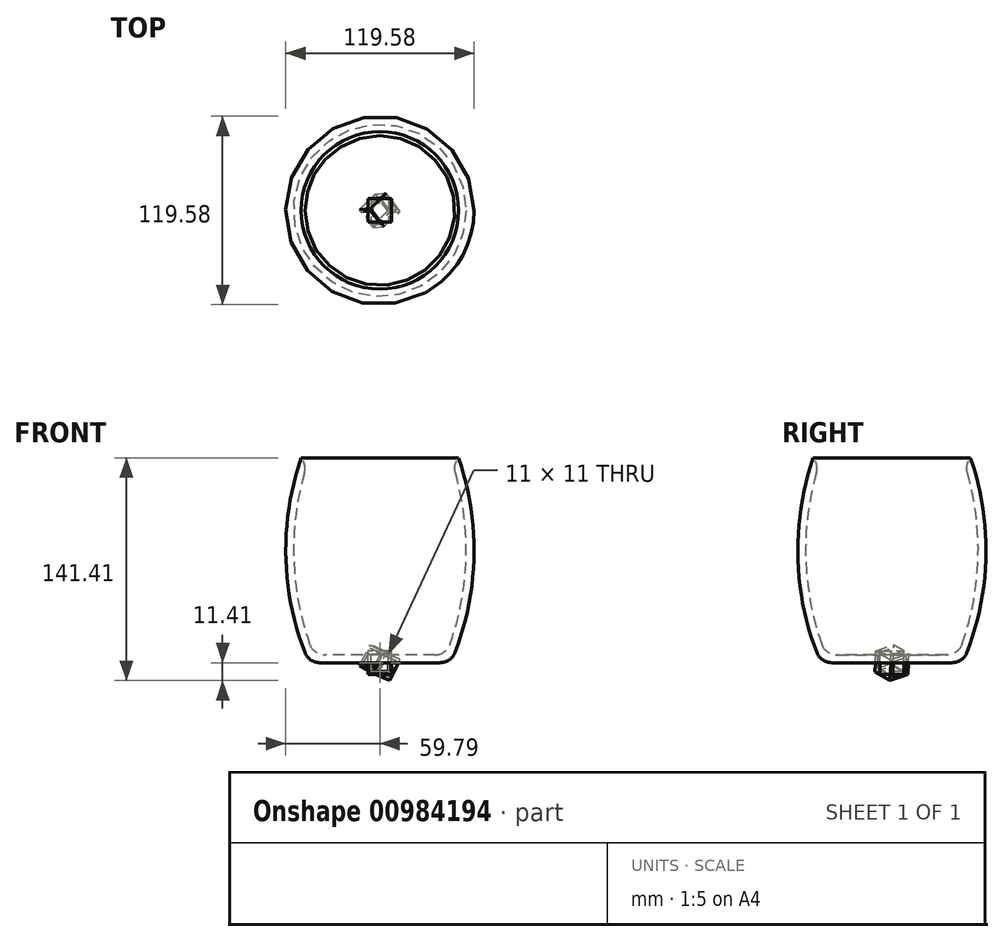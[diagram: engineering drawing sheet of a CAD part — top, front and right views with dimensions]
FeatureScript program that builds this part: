
annotation { "Feature Type Name" : "Feature", "Feature Type Description" : "" }
export const myFeature = defineFeature(function(context is Context, id is Id, definition is map)
    precondition{}
    {
        {
            var Q0;
            Q0=qCreatedBy(makeId("Front.planeOp"),FACE);
            var sketch = newSketch(context, id + "F0", { "sketchPlane" : qUnion([Q0])});
            skLineSegment(sketch, "E0.bottom", {"start": v(7.5, -7.5) * mm, "end": v(-7.5, -7.5) * mm});
            skLineSegment(sketch, "E0.top", {"start": v(7.5, 7.5) * mm, "end": v(-7.5, 7.5) * mm});
            skLineSegment(sketch, "E0.left", {"start": v(7.5, -7.5) * mm, "end": v(7.5, 7.5) * mm});
            skLineSegment(sketch, "E0.right", {"start": v(-7.5, -7.5) * mm, "end": v(-7.5, 7.5) * mm});
            skPoint(sketch, "E0.middle", {"position": v(0, 0) * mm});
            skLineSegment(sketch, "E1.bottom", {"start": v(5.5, -5.5) * mm, "end": v(-5.5, -5.5) * mm});
            skLineSegment(sketch, "E1.top", {"start": v(5.5, 5.5) * mm, "end": v(-5.5, 5.5) * mm});
            skLineSegment(sketch, "E1.left", {"start": v(5.5, -5.5) * mm, "end": v(5.5, 5.5) * mm});
            skLineSegment(sketch, "E1.right", {"start": v(-5.5, -5.5) * mm, "end": v(-5.5, 5.5) * mm});
            skLineSegment(sketch, "E2", {"start": v(0, 0) * mm, "end": v(0, -3) * mm, "construction": true});
            skSolve(sketch);
        }
        {
            var Q0;
            Q0=makeQuery(id+"F0.imprint","IMPRINT",FACE,{"disambiguationData":[TD([[makeQuery(id+"F0.imprint","IMPRINT",EDGE,{"derivedFrom":sQuery(id+"F0.wireOp",EDGE,"E0.bottom")}),-1.0]])]});
            var Q1;
            Q1=makeQuery(id+"F0.imprint","IMPRINT",FACE,{"disambiguationData":[TD([[makeQuery(id+"F0.imprint","IMPRINT",EDGE,{"derivedFrom":sQuery(id+"F0.wireOp",EDGE,"E1.bottom")}),-1.0]])]});
            extrude(context, id + "F1", {"entities" : qUnion([Q0, Q1]), "endBound" : BoundingType.SYMMETRIC, "depth" : 15 * mm, "offsetDistance" : 25 * mm});
        }
        {
            var Q0;
            Q0=makeQuery(id+"F1.opExtrude","CAP_VERTEX",VERTEX,{"disambiguationData":[OSD([sQuery(id+"F0.wireOp",EDGE,"E0.top"),sQuery(id+"F0.wireOp",EDGE,"E0.left")])],"isStart":false});
            var Q1;
            Q1=makeQuery(id+"F1.opExtrude","CAP_VERTEX",VERTEX,{"disambiguationData":[OSD([sQuery(id+"F0.wireOp",EDGE,"E0.bottom"),sQuery(id+"F0.wireOp",EDGE,"E0.right")])],"isStart":true});
            var Q2;
            Q2=makeQuery(id+"F1.opExtrude","CAP_VERTEX",VERTEX,{"disambiguationData":[OSD([sQuery(id+"F0.wireOp",EDGE,"E0.top"),sQuery(id+"F0.wireOp",EDGE,"E0.right")])],"isStart":true});
            cPlane(context, id + "F2", {"entities" : qUnion([Q0, Q1, Q2]), "cplaneType" : CPlaneType.THREE_POINT, "offset" : 25 * mm, "width" : 150 * mm, "height" : 150 * mm});
        }
        {
            var Q0;
            Q0=qCreatedBy(id+"F2.planeOp",FACE);
            var sketch = newSketch(context, id + "F3", { "sketchPlane" : qUnion([Q0])});
            skPoint(sketch, "E3.0", {"position": v(10.6, 7.5) * mm});
            skPoint(sketch, "E4.0", {"position": v(-10.6, -7.5) * mm});
            skLineSegment(sketch, "E5", {"start": v(10.6, 7.5) * mm, "end": v(-10.6, -7.5) * mm, "construction": true});
            skSolve(sketch);
        }
        {
            var Q0;
            Q0=makeQuery(id+"F0.imprint","IMPRINT",FACE,{"disambiguationData":[TD([[makeQuery(id+"F0.imprint","IMPRINT",EDGE,{"derivedFrom":sQuery(id+"F0.wireOp",EDGE,"E1.bottom")}),-1.0]])]});
            extrude(context, id + "F4", {"entities" : qUnion([Q0]), "operationType" : NewBodyOperationType.REMOVE, "endBound" : BoundingType.SYMMETRIC, "oppositeDirection" : true, "depth" : 15 * mm, "offsetDistance" : 25 * mm});
        }
        {
            var Q0;
            Q0=makeQuery(id+"F1.opExtrude","SWEPT_BODY",BODY,{"disambiguationData":[OSD([sQuery(id+"F0.wireOp",EDGE,"E0.bottom"),sQuery(id+"F0.wireOp",EDGE,"E0.top"),sQuery(id+"F0.wireOp",EDGE,"E0.left"),sQuery(id+"F0.wireOp",EDGE,"E0.right")])]});
            var Q1;
            Q1=sQuery(id+"F3.wireOp",EDGE,"E5");
            transform(context, id + "F5", {"entities" : qUnion([Q0]), "transformType" : TransformType.ROTATION, "transformAxis" : qUnion([Q1]), "angle" : 33 * degree, "makeCopy" : true});
        }
        {
            var Q0;
            Q0=makeQuery(id+"F5.opPattern","COPY",BODY,{"derivedFrom":makeQuery(id+"F1.opExtrude","SWEPT_BODY",BODY,{"disambiguationData":[OSD([sQuery(id+"F0.wireOp",EDGE,"E0.bottom"),sQuery(id+"F0.wireOp",EDGE,"E0.top"),sQuery(id+"F0.wireOp",EDGE,"E0.left"),sQuery(id+"F0.wireOp",EDGE,"E0.right")])]}),"instanceName":"1"});
            var Q1;
            Q1=sQuery(id+"F0.wireOp",EDGE,"E2");
            transform(context, id + "F6", {"entities" : qUnion([Q0]), "transformType" : TransformType.ROTATION, "transformAxis" : qUnion([Q1]), "angle" : 30 * degree, "makeCopy" : false});
        }
        {
            var Q0;
            Q0=qCreatedBy(makeId("Front.planeOp"),FACE);
            var sketch = newSketch(context, id + "F7", { "sketchPlane" : qUnion([Q0])});
            skLineSegment(sketch, "E6", {"start": v(0, 0) * mm, "end": v(0, 130) * mm});
            skLineSegment(sketch, "E7", {"start": v(0, 0) * mm, "end": v(45, 0) * mm});
            skArc(sketch, "E8", {"start": v(45, 0) * mm, "mid": v(59.66, 64.53) * mm, "end": v(50, 130) * mm});
            skArc(sketch, "E9", {"start": v(42.07, 5) * mm, "mid": v(54.74, 67.24) * mm, "end": v(45, 130) * mm});
            skLineSegment(sketch, "E10", {"start": v(42.07, 5) * mm, "end": v(0, 5) * mm});
            skLineSegment(sketch, "E11", {"start": v(45, 130) * mm, "end": v(50, 130) * mm});
            skPoint(sketch, "E12.orphan", {"position": v(40, 0) * mm});
            skSolve(sketch);
        }
        {
            var Q0;
            {var subQ0=sQuery(id+"F7.wireOp",EDGE,"E7");Q0=makeQuery(id+"F7.imprint","IMPRINT",FACE,{"disambiguationData":[TD([[makeQuery(id+"F7.imprint","IMPRINT",EDGE,{"derivedFrom":subQ0}),1.0]])]});}
            var Q1;
            Q1=sQuery(id+"F7.wireOp",EDGE,"E6");
            revolve(context, id + "F8", {"surfaceOperationType" : NewSurfaceOperationType.NEW, "entities" : qUnion([Q0]), "axis" : qUnion([Q1]), "revolveType" : RevolveType.FULL});
        }
        {
            var Q0;
            Q0=makeQuery(id+"F8.opRevolve","SWEPT_EDGE",EDGE,{"disambiguationData":[OSD([sQuery(id+"F7.wireOp",EDGE,"E7"),sQuery(id+"F7.wireOp",EDGE,"E8")])]});
            var Q1;
            Q1=makeQuery(id+"F8.opRevolve","SWEPT_EDGE",EDGE,{"disambiguationData":[OSD([sQuery(id+"F7.wireOp",EDGE,"E9"),sQuery(id+"F7.wireOp",EDGE,"E10")])]});
            var Q2;
            Q2=makeQuery(id+"F8.opRevolve","SWEPT_EDGE",EDGE,{"disambiguationData":[OSD([sQuery(id+"F7.wireOp",EDGE,"E9"),sQuery(id+"F7.wireOp",EDGE,"E11")])]});
            fillet(context, id + "F9", {"entities" : qUnion([Q0, Q1, Q2]), "radius" : 10 * mm, "tangentPropagation" : true, "allowEdgeOverflow" : false});
        }
    });
